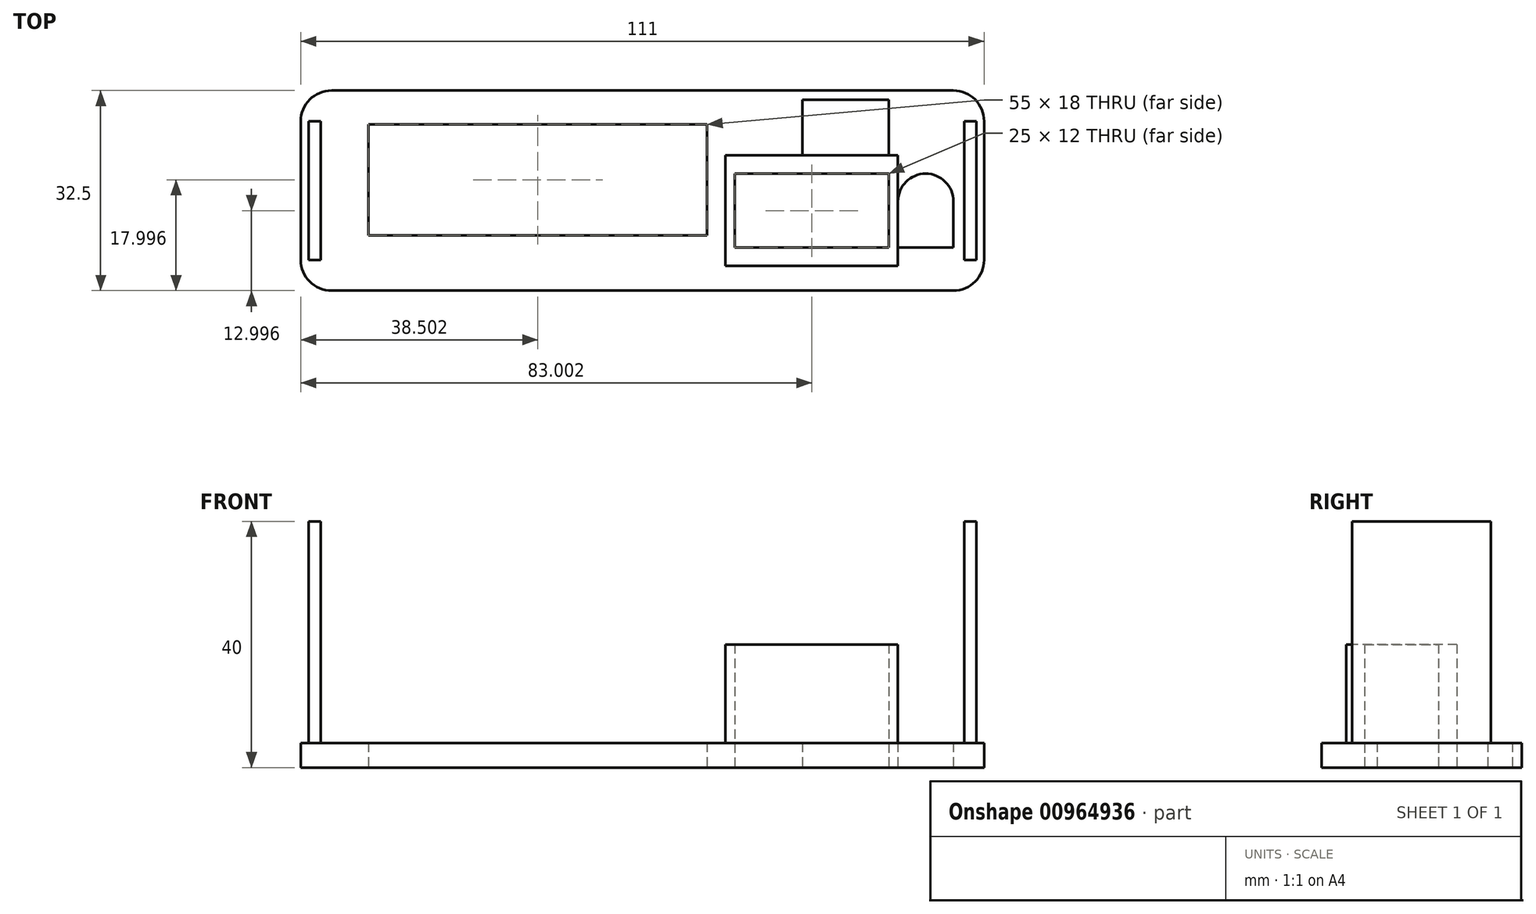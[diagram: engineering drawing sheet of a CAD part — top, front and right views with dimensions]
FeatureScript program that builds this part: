
annotation { "Feature Type Name" : "Feature", "Feature Type Description" : "" }
export const myFeature = defineFeature(function(context is Context, id is Id, definition is map)
    precondition{}
    {
        {
            var Q0;
            Q0=qCreatedBy(makeId("Top.planeOp"),FACE);
            var sketch = newSketch(context, id + "F0", { "sketchPlane" : qUnion([Q0])});
            skLineSegment(sketch, "E0.bottom", {"start": v(-46.6, 14.24) * mm, "end": v(54.4, 14.24) * mm});
            skLineSegment(sketch, "E0.top", {"start": v(-46.6, -18.26) * mm, "end": v(54.4, -18.26) * mm});
            skLineSegment(sketch, "E0.left", {"start": v(-51.6, 9.24) * mm, "end": v(-51.6, -13.26) * mm});
            skLineSegment(sketch, "E0.right", {"start": v(59.4, 9.24) * mm, "end": v(59.4, -13.26) * mm});
            skPoint(sketch, "E1.visualSharp", {"position": v(-51.6, 14.24) * mm});
            skArc(sketch, "E1.filletArc", {"start": v(-46.6, 14.24) * mm, "mid": v(-50.13, 12.77) * mm, "end": v(-51.6, 9.24) * mm});
            skPoint(sketch, "E2.visualSharp", {"position": v(-51.6, -18.26) * mm});
            skArc(sketch, "E2.filletArc", {"start": v(-51.6, -13.26) * mm, "mid": v(-50.13, -16.8) * mm, "end": v(-46.6, -18.26) * mm});
            skPoint(sketch, "E3.visualSharp", {"position": v(59.4, 14.24) * mm});
            skArc(sketch, "E3.filletArc", {"start": v(59.4, 9.24) * mm, "mid": v(57.94, 12.77) * mm, "end": v(54.4, 14.24) * mm});
            skPoint(sketch, "E4.visualSharp", {"position": v(59.4, -18.26) * mm});
            skArc(sketch, "E4.filletArc", {"start": v(54.4, -18.26) * mm, "mid": v(57.94, -16.8) * mm, "end": v(59.4, -13.26) * mm});
            skLineSegment(sketch, "E5.bottom", {"start": v(-40.6, 8.74) * mm, "end": v(14.4, 8.74) * mm});
            skLineSegment(sketch, "E5.top", {"start": v(-40.6, -9.26) * mm, "end": v(14.4, -9.26) * mm});
            skLineSegment(sketch, "E5.left", {"start": v(-40.6, 8.74) * mm, "end": v(-40.6, -9.26) * mm});
            skLineSegment(sketch, "E5.right", {"start": v(14.4, 8.74) * mm, "end": v(14.4, -9.26) * mm});
            skLineSegment(sketch, "E6.bottom", {"start": v(18.9, -11.26) * mm, "end": v(43.9, -11.26) * mm});
            skLineSegment(sketch, "E6.top", {"start": v(18.9, 0.74) * mm, "end": v(43.9, 0.74) * mm});
            skLineSegment(sketch, "E6.left", {"start": v(18.9, -11.26) * mm, "end": v(18.9, 0.74) * mm});
            skLineSegment(sketch, "E6.right", {"start": v(43.9, -11.26) * mm, "end": v(43.9, 0.74) * mm});
            skLineSegment(sketch, "E7.bottom", {"start": v(45.4, -11.26) * mm, "end": v(54.4, -11.26) * mm});
            skLineSegment(sketch, "E7.top", {"start": v(49.9, 0.74) * mm, "end": v(49.9, 0.74) * mm});
            skLineSegment(sketch, "E7.left", {"start": v(45.4, -11.26) * mm, "end": v(45.4, -3.76) * mm});
            skLineSegment(sketch, "E7.right", {"start": v(54.4, -11.26) * mm, "end": v(54.4, -3.76) * mm});
            skLineSegment(sketch, "E8.bottom", {"start": v(29.9, 12.74) * mm, "end": v(43.9, 12.74) * mm});
            skLineSegment(sketch, "E8.top", {"start": v(29.9, 3.74) * mm, "end": v(43.9, 3.74) * mm});
            skLineSegment(sketch, "E8.left", {"start": v(29.9, 12.74) * mm, "end": v(29.9, 3.74) * mm});
            skLineSegment(sketch, "E8.right", {"start": v(43.9, 12.74) * mm, "end": v(43.9, 3.74) * mm});
            skLineSegment(sketch, "E9", {"start": v(17.4, 3.74) * mm, "end": v(29.9, 3.74) * mm});
            skLineSegment(sketch, "E10", {"start": v(43.9, 3.74) * mm, "end": v(45.4, 3.74) * mm});
            skLineSegment(sketch, "E11", {"start": v(45.4, 3.74) * mm, "end": v(45.4, 0.74) * mm});
            skLineSegment(sketch, "E12", {"start": v(45.4, -11.26) * mm, "end": v(45.4, -14.26) * mm});
            skLineSegment(sketch, "E13", {"start": v(45.4, -14.26) * mm, "end": v(18.9, -14.26) * mm});
            skPoint(sketch, "E14.visualSharp", {"position": v(45.4, 0.74) * mm});
            skArc(sketch, "E14.filletArc", {"start": v(49.9, 0.74) * mm, "mid": v(46.72, -0.58) * mm, "end": v(45.4, -3.76) * mm});
            skPoint(sketch, "E15.visualSharp", {"position": v(54.4, 0.74) * mm});
            skArc(sketch, "E15.filletArc", {"start": v(54.4, -3.76) * mm, "mid": v(53.08, -0.58) * mm, "end": v(49.9, 0.74) * mm});
            skLineSegment(sketch, "E16", {"start": v(45.4, 0.74) * mm, "end": v(45.4, -3.76) * mm});
            skPoint(sketch, "E17.start.orphan", {"position": v(14.4, -14.26) * mm});
            skLineSegment(sketch, "E18", {"start": v(17.4, 3.74) * mm, "end": v(17.4, -14.26) * mm});
            skLineSegment(sketch, "E19", {"start": v(17.4, -14.26) * mm, "end": v(18.9, -14.26) * mm});
            skPoint(sketch, "E20.start.orphan", {"position": v(56.9, 6.75) * mm});
            skPoint(sketch, "E21.start.orphan", {"position": v(-51.6, 6.75) * mm});
            skLineSegment(sketch, "E22.bottom", {"start": v(-50.35, 9.24) * mm, "end": v(-48.35, 9.24) * mm});
            skLineSegment(sketch, "E22.top", {"start": v(-50.35, -13.26) * mm, "end": v(-48.35, -13.26) * mm});
            skLineSegment(sketch, "E22.left", {"start": v(-50.35, 9.24) * mm, "end": v(-50.35, -13.26) * mm});
            skLineSegment(sketch, "E22.right", {"start": v(-48.35, 9.24) * mm, "end": v(-48.35, -13.26) * mm});
            skLineSegment(sketch, "E23.bottom", {"start": v(58.15, 9.24) * mm, "end": v(56.15, 9.24) * mm});
            skLineSegment(sketch, "E23.top", {"start": v(58.15, -13.26) * mm, "end": v(56.15, -13.26) * mm});
            skLineSegment(sketch, "E23.left", {"start": v(58.15, 9.24) * mm, "end": v(58.15, -13.26) * mm});
            skLineSegment(sketch, "E23.right", {"start": v(56.15, 9.24) * mm, "end": v(56.15, -13.26) * mm});
            skSolve(sketch);
        }
        {
            var Q0;
            Q0=makeQuery(id+"F0.imprint","IMPRINT",FACE,{"disambiguationData":[TD([[makeQuery(id+"F0.imprint","IMPRINT",EDGE,{"derivedFrom":sQuery(id+"F0.wireOp",EDGE,"E0.bottom")}),-1.0]])]});
            extrude(context, id + "F1", {"entities" : qUnion([Q0]), "depth" : 4 * mm, "offsetDistance" : 25 * mm});
        }
        {
            var Q0;
            Q0=makeQuery(id+"F0.imprint","IMPRINT",FACE,{"disambiguationData":[TD([[makeQuery(id+"F0.imprint","IMPRINT",EDGE,{"derivedFrom":sQuery(id+"F0.wireOp",EDGE,"E6.bottom")}),-1.0]])]});
            extrude(context, id + "F2", {"entities" : qUnion([Q0]), "operationType" : NewBodyOperationType.ADD, "depth" : 20 * mm, "offsetDistance" : 25 * mm});
        }
        {
            var Q0;
            Q0=makeQuery(id+"F0.imprint","IMPRINT",FACE,{"disambiguationData":[TD([[makeQuery(id+"F0.imprint","IMPRINT",EDGE,{"derivedFrom":sQuery(id+"F0.wireOp",EDGE,"E23.bottom")}),1.0]])]});
            var Q1;
            Q1=makeQuery(id+"F0.imprint","IMPRINT",FACE,{"disambiguationData":[TD([[makeQuery(id+"F0.imprint","IMPRINT",EDGE,{"derivedFrom":sQuery(id+"F0.wireOp",EDGE,"E22.bottom")}),-1.0]])]});
            extrude(context, id + "F3", {"entities" : qUnion([Q0, Q1]), "operationType" : NewBodyOperationType.ADD, "depth" : 40 * mm, "offsetDistance" : 25 * mm});
        }
    });
